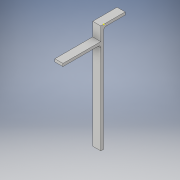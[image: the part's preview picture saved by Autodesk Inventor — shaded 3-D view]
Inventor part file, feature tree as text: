
AUTODESK INVENTOR PART (.ipt)
format: ipt  version: 2017 (Build 210142000, 142)  size: 122,368 bytes
history: native  units: in
note: dims shown in document units (in); Inventor stores cm internally (conversion verified against a paired STEP export)
features: sketch x4, extrude x3, fillet x1
ambient origin geometry x8: Origin, YZ Plane, XZ Plane, XY Plane, X Axis, Y Axis, Z Axis, Center Point
bodies: Solid1 (feature_tree)
feature tree (8):
  extrude  "Extrusion1"  Depth=10.0in
  sketch  "Sketch4"  dims[d2=0.25in d3=0.0in d4=1.25in]
  extrude  "Extrusion2"  Depth=1.25in
  extrude  "Extrusion3"  Depth=3.5in TaperAngle=0.0deg
  fillet  "Fillet2"  Radius=0.25in
  sketch  "Sketch3"  dims[d0=0.75in d1=10.0in]
  sketch  "Sketch5"  dims[d5=0.25in d6=3.5in d7=0.0in d8=0.25in]
  sketch  "Sketch6"  dims[d9=2.0in d10=0.0in d12=0.25in]
